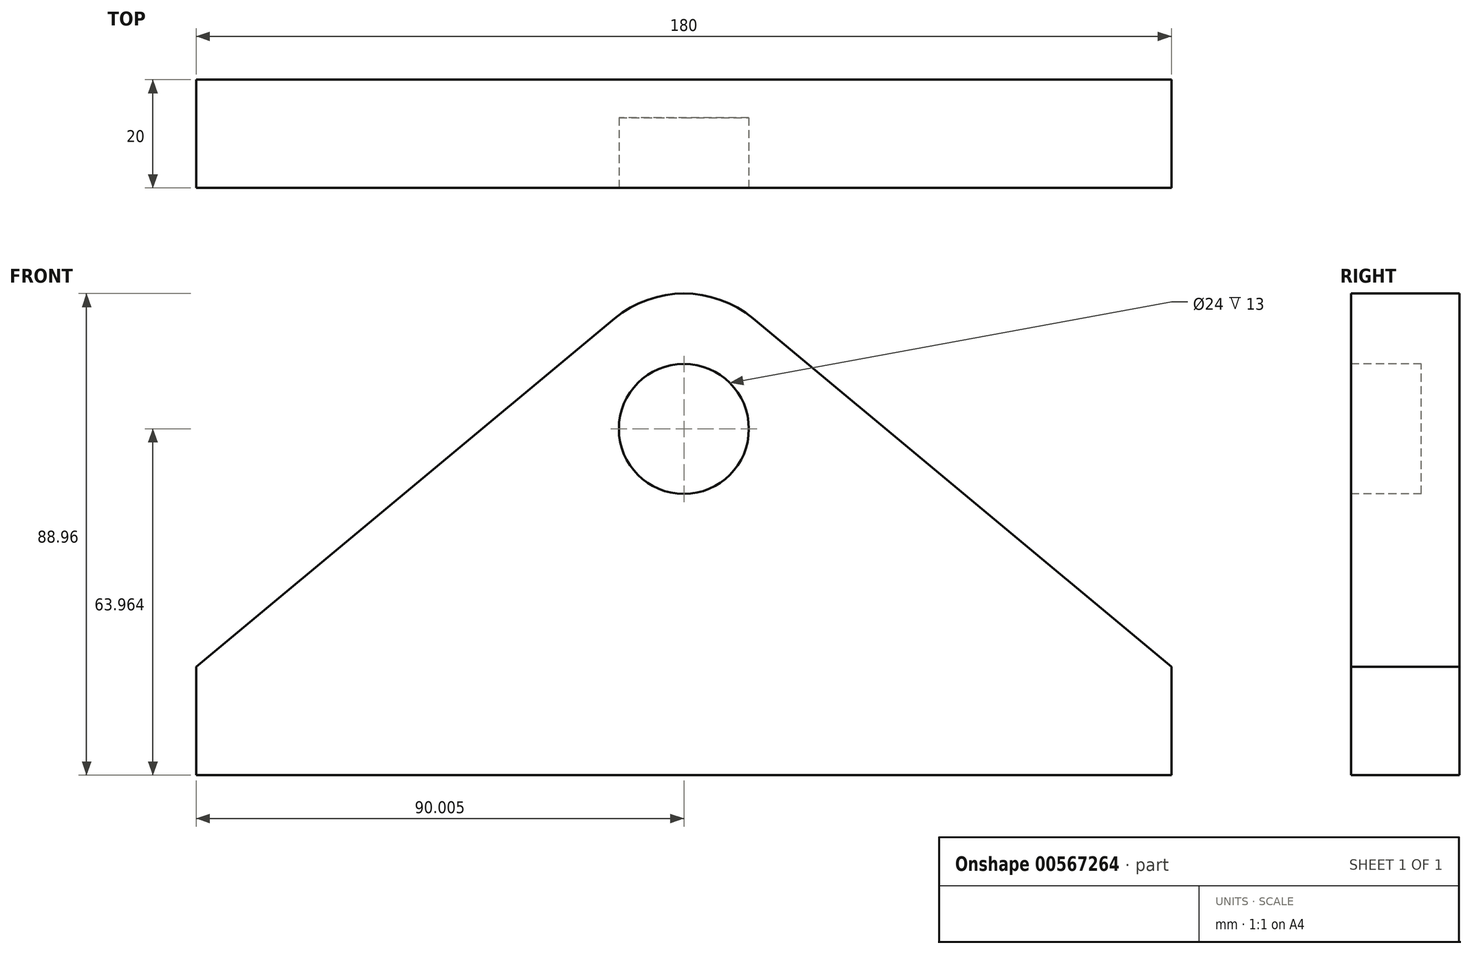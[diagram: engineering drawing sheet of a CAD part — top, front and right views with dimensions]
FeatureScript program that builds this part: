
annotation { "Feature Type Name" : "Feature", "Feature Type Description" : "" }
export const myFeature = defineFeature(function(context is Context, id is Id, definition is map)
    precondition{}
    {
        {
            var Q0;
            Q0=qCreatedBy(makeId("Front.planeOp"),FACE);
            var sketch = newSketch(context, id + "F0", { "sketchPlane" : qUnion([Q0])});
            skLineSegment(sketch, "E0.top", {"start": v(-98.78, -29.2) * mm, "end": v(81.22, -29.2) * mm});
            skLineSegment(sketch, "E1", {"start": v(81.22, 70.8) * mm, "end": v(81.22, 65.8) * mm});
            skLineSegment(sketch, "E2", {"start": v(-98.78, -29.2) * mm, "end": v(-98.78, -9.2) * mm});
            skLineSegment(sketch, "E3", {"start": v(81.22, -29.2) * mm, "end": v(81.22, -9.2) * mm});
            skLineSegment(sketch, "E4", {"start": v(-98.78, -9.2) * mm, "end": v(-21.58, 55.14) * mm});
            skLineSegment(sketch, "E5", {"start": v(4.03, 55.14) * mm, "end": v(81.22, -9.2) * mm});
            skPoint(sketch, "E6.visualSharp", {"position": v(-8.78, 65.8) * mm});
            skArc(sketch, "E6.filletArc", {"start": v(4.03, 55.14) * mm, "mid": v(-8.78, 59.77) * mm, "end": v(-21.58, 55.14) * mm});
            skLineSegment(sketch, "E7", {"start": v(-8.78, 59.77) * mm, "end": v(-8.78, 34.77) * mm});
            skSolve(sketch);
        }
        {
            var Q0;
            Q0=qSketchRegion(id+"F0",true);
            extrude(context, id + "F1", {"entities" : qUnion([Q0]), "depth" : 20 * mm, "offsetDistance" : 25 * mm});
        }
        {
            var Q0;
            Q0=makeQuery(id+"F1.opExtrude","CAP_FACE",FACE,{"disambiguationData":[OSD([sQuery(id+"F0.wireOp",EDGE,"E0.top"),sQuery(id+"F0.wireOp",EDGE,"E2"),sQuery(id+"F0.wireOp",EDGE,"E3"),sQuery(id+"F0.wireOp",EDGE,"E4"),sQuery(id+"F0.wireOp",EDGE,"E5"),sQuery(id+"F0.wireOp",EDGE,"E6.filletArc")])],"isStart":false});
            var sketch = newSketch(context, id + "F2", { "sketchPlane" : qUnion([Q0])});
            skLineSegment(sketch, "E8", {"start": v(-8.78, 59.77) * mm, "end": v(-8.78, 34.77) * mm});
            skCircle(sketch, "E9", {"center": v(-8.78, 34.77) * mm, "radius": 12 * mm});
            skSolve(sketch);
        }
        {
            var Q0;
            Q0=makeQuery(id+"F2.imprint","IMPRINT",FACE,{"disambiguationData":[TD([[makeQuery(id+"F2.imprint","IMPRINT",EDGE,{"derivedFrom":sQuery(id+"F2.wireOp",EDGE,"E9")}),1.0]])]});
            extrude(context, id + "F3", {"entities" : qUnion([Q0]), "operationType" : NewBodyOperationType.REMOVE, "oppositeDirection" : true, "depth" : 13 * mm, "offsetDistance" : 25 * mm});
        }
    });
